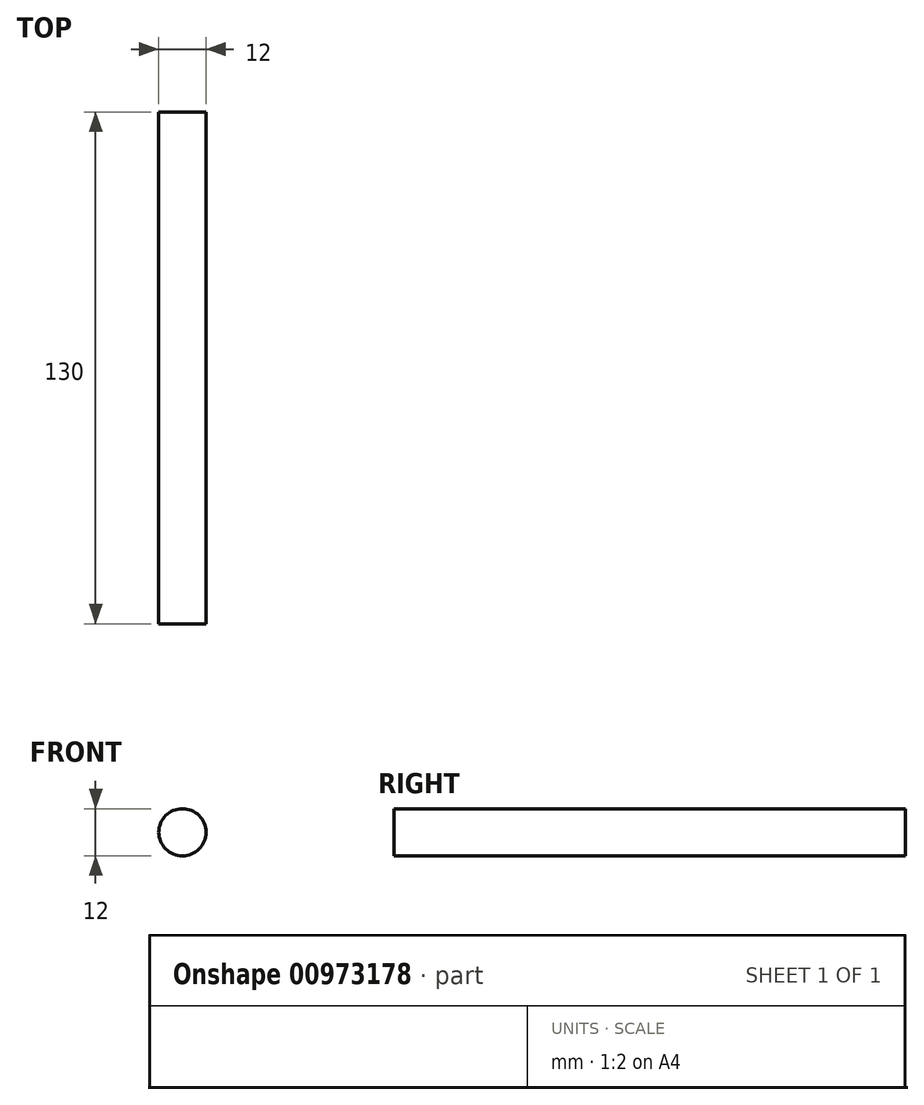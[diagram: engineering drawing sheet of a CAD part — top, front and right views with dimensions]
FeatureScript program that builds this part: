
annotation { "Feature Type Name" : "Feature", "Feature Type Description" : "" }
export const myFeature = defineFeature(function(context is Context, id is Id, definition is map)
    precondition{}
    {
        {
            var Q0;
            Q0=qCreatedBy(makeId("Front.planeOp"),FACE);
            var sketch = newSketch(context, id + "F0", { "sketchPlane" : qUnion([Q0])});
            skCircle(sketch, "E0", {"center": v(0, 0) * mm, "radius": 6 * mm});
            skSolve(sketch);
        }
        {
            var Q0;
            Q0=makeQuery(id+"F0.imprint","IMPRINT",FACE,{"disambiguationData":[TD([[makeQuery(id+"F0.imprint","IMPRINT",EDGE,{"derivedFrom":sQuery(id+"F0.wireOp",EDGE,"E0")}),1.0]])]});
            extrude(context, id + "F1", {"entities" : qUnion([Q0]), "depth" : 130 * mm, "offsetDistance" : 25 * mm});
        }
    });
